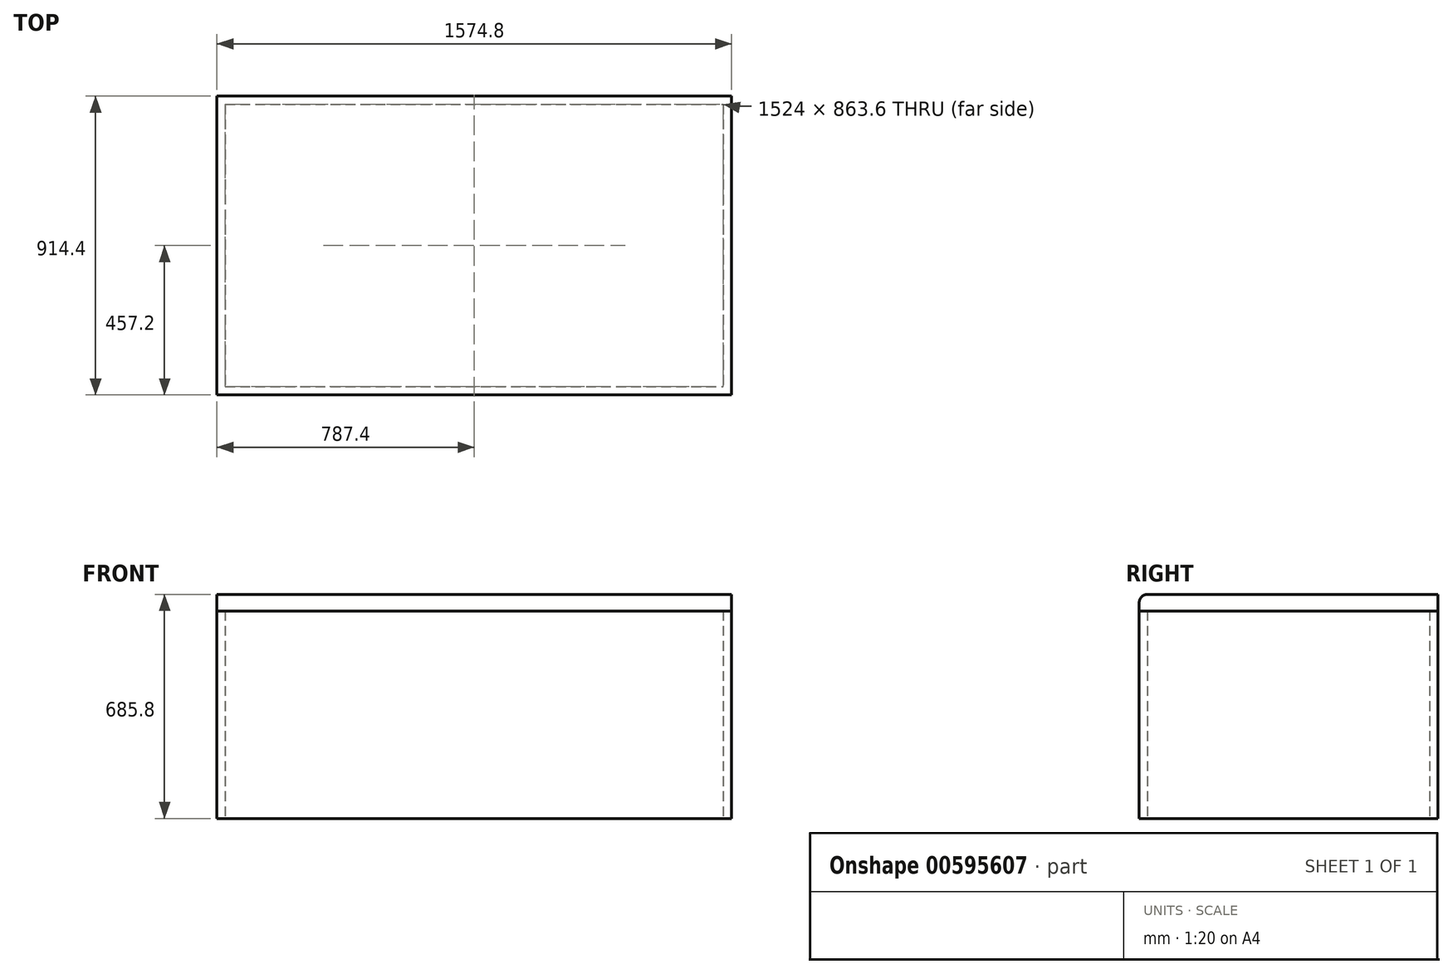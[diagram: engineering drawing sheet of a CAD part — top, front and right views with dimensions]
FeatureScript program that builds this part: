
annotation { "Feature Type Name" : "Feature", "Feature Type Description" : "" }
export const myFeature = defineFeature(function(context is Context, id is Id, definition is map)
    precondition{}
    {
        {
            var Q0;
            Q0=qCreatedBy(makeId("Top.planeOp"),FACE);
            var sketch = newSketch(context, id + "F0", { "sketchPlane" : qUnion([Q0])});
            skLineSegment(sketch, "E0.bottom", {"start": v(-787.4, 457.2) * mm, "end": v(787.4, 457.2) * mm});
            skLineSegment(sketch, "E0.top", {"start": v(-787.4, -457.2) * mm, "end": v(787.4, -457.2) * mm});
            skLineSegment(sketch, "E0.left", {"start": v(-787.4, 457.2) * mm, "end": v(-787.4, -457.2) * mm});
            skLineSegment(sketch, "E0.right", {"start": v(787.4, 457.2) * mm, "end": v(787.4, -457.2) * mm});
            skPoint(sketch, "E0.middle", {"position": v(0, 0) * mm});
            skLineSegment(sketch, "E1.bottom", {"start": v(-762, 431.8) * mm, "end": v(762, 431.8) * mm});
            skLineSegment(sketch, "E1.top", {"start": v(-762, -431.8) * mm, "end": v(762, -431.8) * mm});
            skLineSegment(sketch, "E1.left", {"start": v(-762, 431.8) * mm, "end": v(-762, -431.8) * mm});
            skLineSegment(sketch, "E1.right", {"start": v(762, 431.8) * mm, "end": v(762, -431.8) * mm});
            skSolve(sketch);
        }
        {
            var Q0;
            Q0=makeQuery(id+"F0.imprint","IMPRINT",FACE,{"disambiguationData":[TD([[makeQuery(id+"F0.imprint","IMPRINT",EDGE,{"derivedFrom":sQuery(id+"F0.wireOp",EDGE,"E0.bottom")}),-1.0]])]});
            extrude(context, id + "F1", {"entities" : qUnion([Q0]), "depth" : 635 * mm, "offsetDistance" : 25.4 * mm});
        }
        {
            var Q0;
            Q0=makeQuery(id+"F1.opExtrude","CAP_FACE",FACE,{"disambiguationData":[OSD([sQuery(id+"F0.wireOp",EDGE,"E0.bottom"),sQuery(id+"F0.wireOp",EDGE,"E0.top"),sQuery(id+"F0.wireOp",EDGE,"E0.left"),sQuery(id+"F0.wireOp",EDGE,"E0.right"),sQuery(id+"F0.wireOp",EDGE,"E1.bottom"),sQuery(id+"F0.wireOp",EDGE,"E1.top"),sQuery(id+"F0.wireOp",EDGE,"E1.left"),sQuery(id+"F0.wireOp",EDGE,"E1.right")])],"isStart":false});
            var sketch = newSketch(context, id + "F2", { "sketchPlane" : qUnion([Q0])});
            skLineSegment(sketch, "E2.bottom", {"start": v(-787.4, 457.2) * mm, "end": v(787.4, 457.2) * mm});
            skLineSegment(sketch, "E2.top", {"start": v(-787.4, -457.2) * mm, "end": v(787.4, -457.2) * mm});
            skLineSegment(sketch, "E2.left", {"start": v(-787.4, 457.2) * mm, "end": v(-787.4, -457.2) * mm});
            skLineSegment(sketch, "E2.right", {"start": v(787.4, 457.2) * mm, "end": v(787.4, -457.2) * mm});
            skSolve(sketch);
        }
        {
            var Q0;
            Q0 = qSketchRegion(id + "F2", true);
            extrude(context, id + "F3", {"entities" : qUnion([Q0]), "depth" : 50.8 * mm, "offsetDistance" : 25.4 * mm});
        }
        {
            var Q0;
            Q0=makeQuery(id+"F3.opExtrude","CAP_EDGE",EDGE,{"disambiguationData":[OSD([sQuery(id+"F2.wireOp",EDGE,"E2.top")])],"isStart":false});
            fillet(context, id + "F4", {"entities" : qUnion([Q0]), "radius" : 25.4 * mm, "tangentPropagation" : true, "allowEdgeOverflow" : false});
        }
    });
